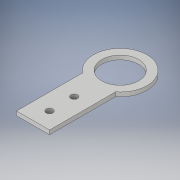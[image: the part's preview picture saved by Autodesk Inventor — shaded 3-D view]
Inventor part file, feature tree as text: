
AUTODESK INVENTOR PART (.ipt)
format: ipt  version: 2018 (Build 220112000, 112)  size: 116,224 bytes
history: native  units: in
note: dims shown in document units (in); Inventor stores cm internally (conversion verified against a paired STEP export)
features: extrude x1, sketch x1
ambient origin geometry x8: Origin, YZ Plane, XZ Plane, XY Plane, X Axis, Y Axis, Z Axis, Center Point
bodies: Solid1 (feature_tree)
feature tree (2):
  extrude  "Extrusion1"  Depth=2.0in
  sketch  "Sketch1"  dims[d0=1.0in d1=2.0in d2=1.125in d3=0.25in d4=0.5in d5=0.75in d6=0.2031in d7=0.2031in d8=0.125in d9=0.0in]
